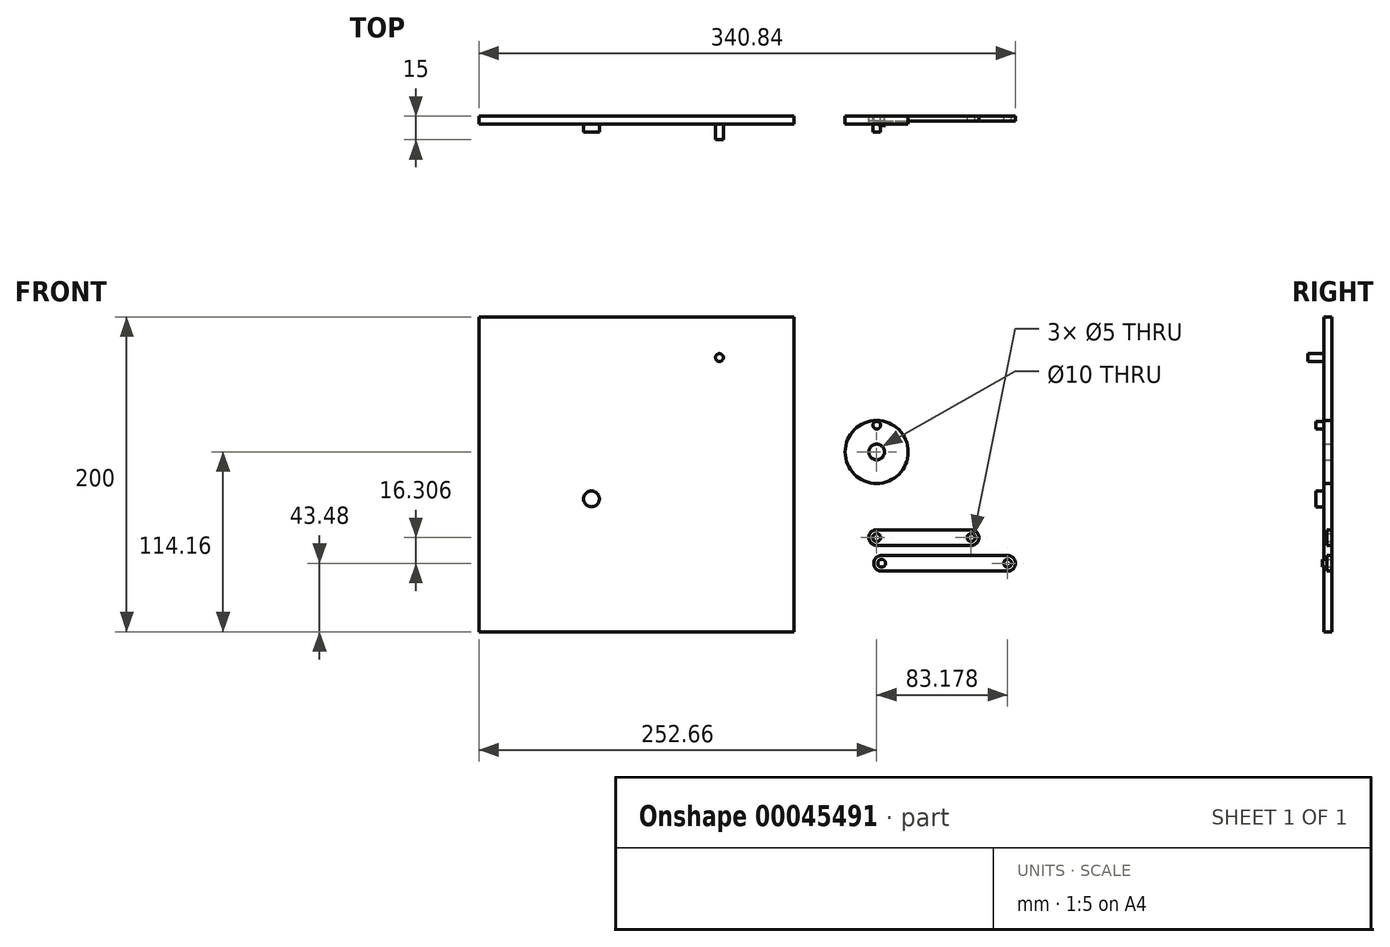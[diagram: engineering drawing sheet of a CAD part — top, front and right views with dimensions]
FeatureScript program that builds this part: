
annotation { "Feature Type Name" : "Feature", "Feature Type Description" : "" }
export const myFeature = defineFeature(function(context is Context, id is Id, definition is map)
    precondition{}
    {
        {
            var Q0;
            Q0=qCreatedBy(makeId("Front.planeOp"),FACE);
            var sketch = newSketch(context, id + "F0", { "sketchPlane" : qUnion([Q0])});
            skCircle(sketch, "E0", {"center": v(0, 0) * mm, "radius": 20 * mm});
            skCircle(sketch, "E1", {"center": v(0, 0) * mm, "radius": 5 * mm});
            skSolve(sketch);
        }
        {
            var Q0;
            Q0=makeQuery(id+"F0.imprint","IMPRINT",FACE,{"disambiguationData":[TD([[makeQuery(id+"F0.imprint","IMPRINT",EDGE,{"derivedFrom":sQuery(id+"F0.wireOp",EDGE,"E0")}),1.0]])]});
            extrude(context, id + "F1", {"entities" : qUnion([Q0]), "depth" : 5 * mm});
        }
        {
            var Q0;
            Q0=qCreatedBy(makeId("Front.planeOp"),FACE);
            var sketch = newSketch(context, id + "F2", { "sketchPlane" : qUnion([Q0])});
            skLineSegment(sketch, "E2.bottom", {"start": v(-52.66, -114.16) * mm, "end": v(-252.66, -114.16) * mm});
            skLineSegment(sketch, "E2.top", {"start": v(-52.66, 85.84) * mm, "end": v(-252.66, 85.84) * mm});
            skLineSegment(sketch, "E2.left", {"start": v(-52.66, -114.16) * mm, "end": v(-52.66, 85.84) * mm});
            skLineSegment(sketch, "E2.right", {"start": v(-252.66, -114.16) * mm, "end": v(-252.66, 85.84) * mm});
            skCircle(sketch, "E3", {"center": v(-181.12, -29.8) * mm, "radius": 5 * mm});
            skCircle(sketch, "E4", {"center": v(-99.86, 59.97) * mm, "radius": 2.5 * mm});
            skSolve(sketch);
        }
        {
            var Q0;
            Q0 = qSketchRegion(id + "F2", true);
            extrude(context, id + "F3", {"entities" : qUnion([Q0]), "depth" : 5 * mm});
        }
        {
            var Q0;
            Q0=makeQuery(id+"F2.imprint","IMPRINT",FACE,{"disambiguationData":[TD([[makeQuery(id+"F2.imprint","IMPRINT",EDGE,{"derivedFrom":sQuery(id+"F2.wireOp",EDGE,"E3")}),1.0]])]});
            extrude(context, id + "F4", {"entities" : qUnion([Q0]), "operationType" : NewBodyOperationType.ADD, "depth" : 10 * mm});
        }
        {
            var Q0;
            Q0=makeQuery(id+"F1.opExtrude","CAP_FACE",FACE,{"disambiguationData":[OSD([sQuery(id+"F0.wireOp",EDGE,"E0"),sQuery(id+"F0.wireOp",EDGE,"E1")])],"isStart":false});
            var sketch = newSketch(context, id + "F5", { "sketchPlane" : qUnion([Q0])});
            skCircle(sketch, "E5", {"center": v(0.05, 17.02) * mm, "radius": 2.42 * mm});
            skSolve(sketch);
        }
        {
            var Q0;
            Q0=makeQuery(id+"F5.imprint","IMPRINT",FACE,{"disambiguationData":[TD([[makeQuery(id+"F5.imprint","IMPRINT",EDGE,{"derivedFrom":sQuery(id+"F5.wireOp",EDGE,"E5")}),1.0]])]});
            extrude(context, id + "F6", {"entities" : qUnion([Q0]), "operationType" : NewBodyOperationType.ADD, "depth" : 5 * mm});
        }
        {
            var Q0;
            Q0=qCreatedBy(makeId("Front.planeOp"),FACE);
            var sketch = newSketch(context, id + "F7", { "sketchPlane" : qUnion([Q0])});
            skLineSegment(sketch, "E6.bottom", {"start": v(0, -49.37) * mm, "end": v(60, -49.37) * mm});
            skLineSegment(sketch, "E6.top", {"start": v(0, -59.37) * mm, "end": v(60, -59.37) * mm});
            skLineSegment(sketch, "E6.left", {"start": v(-5, -54.37) * mm, "end": v(-5, -54.37) * mm});
            skLineSegment(sketch, "E6.right", {"start": v(65, -54.37) * mm, "end": v(65, -54.37) * mm});
            skCircle(sketch, "E7", {"center": v(0, -54.37) * mm, "radius": 2.5 * mm});
            skCircle(sketch, "E8", {"center": v(60, -54.37) * mm, "radius": 2.5 * mm});
            skPoint(sketch, "E9.visualSharp", {"position": v(-5, -49.37) * mm});
            skArc(sketch, "E9.filletArc", {"start": v(0, -49.37) * mm, "mid": v(-3.54, -50.84) * mm, "end": v(-5, -54.37) * mm});
            skPoint(sketch, "E10.visualSharp", {"position": v(-5, -59.37) * mm});
            skArc(sketch, "E10.filletArc", {"start": v(-5, -54.37) * mm, "mid": v(-3.54, -57.91) * mm, "end": v(0, -59.37) * mm});
            skPoint(sketch, "E11.visualSharp", {"position": v(65, -59.37) * mm});
            skArc(sketch, "E11.filletArc", {"start": v(60, -59.37) * mm, "mid": v(63.54, -57.91) * mm, "end": v(65, -54.37) * mm});
            skPoint(sketch, "E12.visualSharp", {"position": v(65, -49.37) * mm});
            skArc(sketch, "E12.filletArc", {"start": v(65, -54.37) * mm, "mid": v(63.54, -50.84) * mm, "end": v(60, -49.37) * mm});
            skSolve(sketch);
        }
        {
            var Q0;
            Q0=qCreatedBy(makeId("Front.planeOp"),FACE);
            var sketch = newSketch(context, id + "F8", { "sketchPlane" : qUnion([Q0])});
            skLineSegment(sketch, "E13.bottom", {"start": v(3.18, -65.68) * mm, "end": v(83.18, -65.68) * mm});
            skLineSegment(sketch, "E13.top", {"start": v(3.18, -75.68) * mm, "end": v(83.18, -75.68) * mm});
            skLineSegment(sketch, "E13.left", {"start": v(-1.82, -70.68) * mm, "end": v(-1.82, -70.68) * mm});
            skLineSegment(sketch, "E13.right", {"start": v(88.18, -70.68) * mm, "end": v(88.18, -70.68) * mm});
            skCircle(sketch, "E14", {"center": v(3.18, -70.68) * mm, "radius": 2.5 * mm});
            skPoint(sketch, "E15.visualSharp", {"position": v(-1.82, -65.68) * mm});
            skArc(sketch, "E15.filletArc", {"start": v(3.18, -65.68) * mm, "mid": v(-0.36, -67.14) * mm, "end": v(-1.82, -70.68) * mm});
            skPoint(sketch, "E16.visualSharp", {"position": v(-1.82, -75.68) * mm});
            skArc(sketch, "E16.filletArc", {"start": v(-1.82, -70.68) * mm, "mid": v(-0.36, -74.22) * mm, "end": v(3.18, -75.68) * mm});
            skCircle(sketch, "E17", {"center": v(83.18, -70.68) * mm, "radius": 2.5 * mm});
            skPoint(sketch, "E18.visualSharp", {"position": v(88.18, -65.68) * mm});
            skArc(sketch, "E18.filletArc", {"start": v(88.18, -70.68) * mm, "mid": v(86.71, -67.14) * mm, "end": v(83.18, -65.68) * mm});
            skPoint(sketch, "E19.visualSharp", {"position": v(88.18, -75.68) * mm});
            skArc(sketch, "E19.filletArc", {"start": v(83.18, -75.68) * mm, "mid": v(86.71, -74.22) * mm, "end": v(88.18, -70.68) * mm});
            skSolve(sketch);
        }
        {
            var Q0;
            Q0 = qSketchRegion(id + "F7", true);
            extrude(context, id + "F9", {"entities" : qUnion([Q0]), "depth" : 3 * mm});
        }
        {
            var Q0;
            Q0 = qSketchRegion(id + "F8", true);
            extrude(context, id + "F10", {"entities" : qUnion([Q0]), "depth" : 3 * mm});
        }
        {
            var Q0;
            Q0=makeQuery(id+"F8.imprint","IMPRINT",FACE,{"disambiguationData":[TD([[makeQuery(id+"F8.imprint","IMPRINT",EDGE,{"derivedFrom":sQuery(id+"F8.wireOp",EDGE,"E14")}),1.0]])]});
            extrude(context, id + "F11", {"entities" : qUnion([Q0]), "operationType" : NewBodyOperationType.ADD, "depth" : 6 * mm});
        }
        {
            var Q0;
            Q0=makeQuery(id+"F2.imprint","IMPRINT",FACE,{"disambiguationData":[TD([[makeQuery(id+"F2.imprint","IMPRINT",EDGE,{"derivedFrom":sQuery(id+"F2.wireOp",EDGE,"E4")}),1.0]])]});
            extrude(context, id + "F12", {"entities" : qUnion([Q0]), "operationType" : NewBodyOperationType.ADD, "depth" : 15 * mm});
        }
    });
